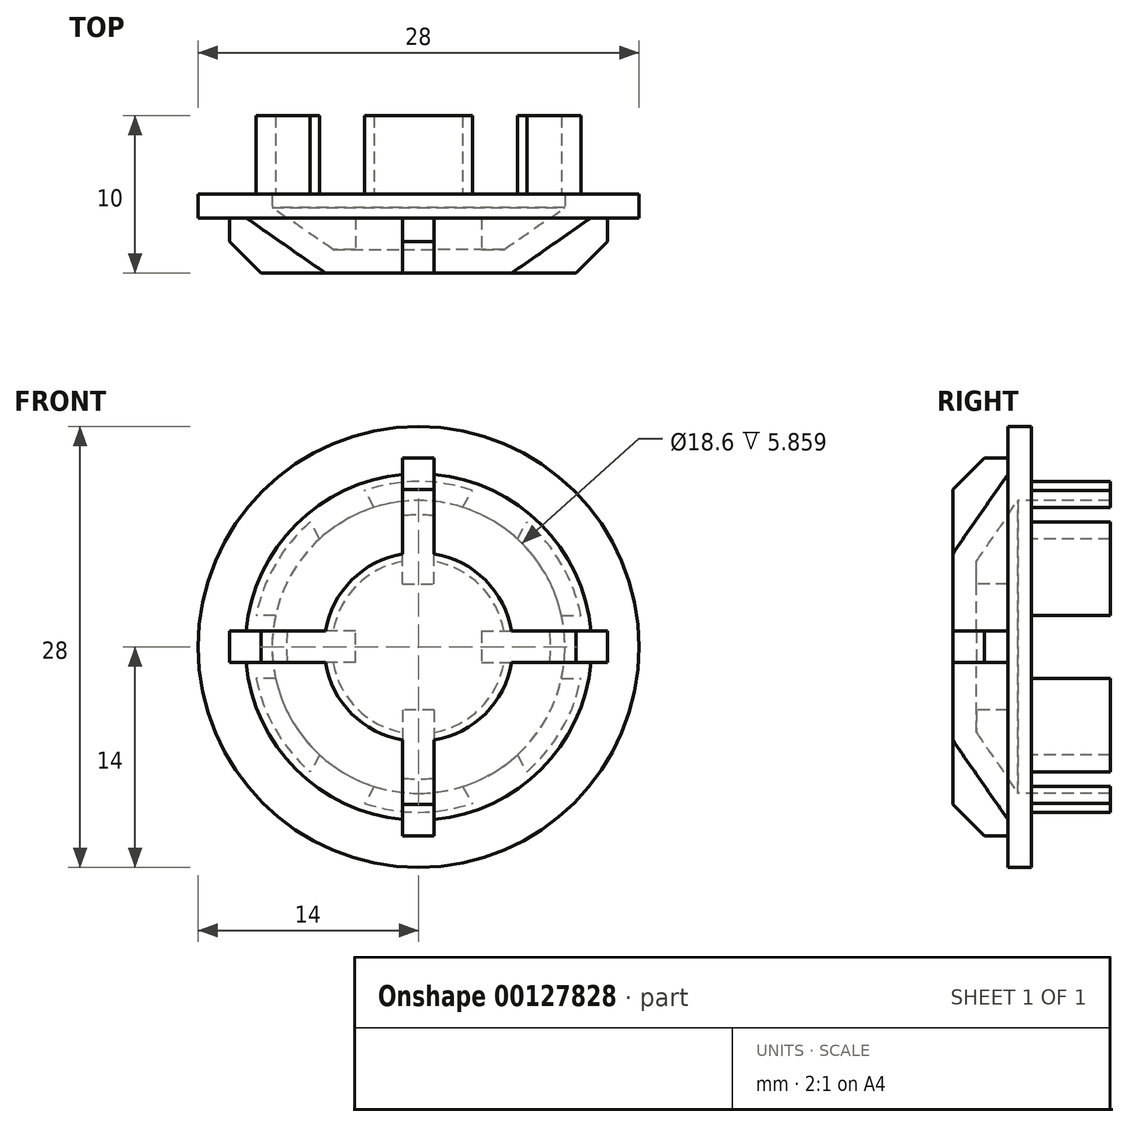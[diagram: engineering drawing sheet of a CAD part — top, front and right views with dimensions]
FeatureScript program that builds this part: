
annotation { "Feature Type Name" : "Feature", "Feature Type Description" : "" }
export const myFeature = defineFeature(function(context is Context, id is Id, definition is map)
    precondition{}
    {
        {
            var Q0;
            Q0=qCreatedBy(makeId("Top.planeOp"),FACE);
            var sketch = newSketch(context, id + "F0", { "sketchPlane" : qUnion([Q0])});
            skLineSegment(sketch, "E0", {"start": v(0, 0) * mm, "end": v(6, 0) * mm});
            skLineSegment(sketch, "E1", {"start": v(6, 0) * mm, "end": v(11, 3.5) * mm});
            skLineSegment(sketch, "E2", {"start": v(11, 3.5) * mm, "end": v(14, 3.5) * mm});
            skLineSegment(sketch, "E3", {"start": v(14, 3.5) * mm, "end": v(14, 5) * mm});
            skLineSegment(sketch, "E4", {"start": v(14, 5) * mm, "end": v(10.5, 5) * mm});
            skLineSegment(sketch, "E5", {"start": v(10.5, 5) * mm, "end": v(10.5, 10) * mm});
            skLineSegment(sketch, "E6", {"start": v(10.5, 10) * mm, "end": v(9.3, 10) * mm});
            skLineSegment(sketch, "E7", {"start": v(9.3, 10) * mm, "end": v(9.3, 4.14) * mm});
            skLineSegment(sketch, "E8", {"start": v(9.3, 4.14) * mm, "end": v(5.53, 1.5) * mm});
            skLineSegment(sketch, "E9", {"start": v(5.53, 1.5) * mm, "end": v(0, 1.5) * mm});
            skLineSegment(sketch, "E10", {"start": v(0, 1.5) * mm, "end": v(0, 0) * mm});
            skLineSegment(sketch, "E11", {"start": v(0, 0) * mm, "end": v(0, 11.38) * mm, "construction": true});
            skSolve(sketch);
        }
        {
            var Q0;
            Q0 = qSketchRegion(id + "F0", true);
            var Q1;
            Q1 = qConstructionFilter(qBodyType(qCreatedBy(id + "F0" ,EDGE), BodyType.WIRE), ConstructionObject.NO);
            var Q2;
            Q2=sQuery(id+"F0.wireOp",EDGE,"E11");
            revolve(context, id + "F1", {"entities" : qUnion([Q0]), "surfaceEntities" : qUnion([Q1]), "axis" : qUnion([Q2]), "revolveType" : RevolveType.FULL});
        }
        {
            var Q0;
            Q0=makeQuery(id+"F1.opRevolve","SWEPT_FACE",FACE,{"disambiguationData":[OSD([sQuery(id+"F0.wireOp",EDGE,"E6")])]});
            var sketch = newSketch(context, id + "F2", { "sketchPlane" : qUnion([Q0])});
            skLineSegment(sketch, "E12.bottom", {"start": v(7.95, 2) * mm, "end": v(11.94, 2) * mm});
            skLineSegment(sketch, "E12.top", {"start": v(7.95, -2) * mm, "end": v(11.94, -2) * mm});
            skLineSegment(sketch, "E12.left", {"start": v(7.95, 2) * mm, "end": v(7.95, -2) * mm});
            skLineSegment(sketch, "E12.right", {"start": v(11.94, 2) * mm, "end": v(11.94, -2) * mm});
            skLineSegment(sketch, "E13.1.0", {"start": v(2.24, 7.88) * mm, "end": v(4.24, 11.34) * mm});
            skLineSegment(sketch, "E13.1.1", {"start": v(5.7, 5.88) * mm, "end": v(7.7, 9.34) * mm});
            skLineSegment(sketch, "E13.1.2", {"start": v(2.24, 7.88) * mm, "end": v(5.7, 5.88) * mm});
            skLineSegment(sketch, "E13.1.3", {"start": v(4.24, 11.34) * mm, "end": v(7.7, 9.34) * mm});
            skLineSegment(sketch, "E13.2.0", {"start": v(-5.7, 5.88) * mm, "end": v(-7.7, 9.34) * mm});
            skLineSegment(sketch, "E13.2.1", {"start": v(-2.24, 7.88) * mm, "end": v(-4.24, 11.34) * mm});
            skLineSegment(sketch, "E13.2.2", {"start": v(-5.7, 5.88) * mm, "end": v(-2.24, 7.88) * mm});
            skLineSegment(sketch, "E13.2.3", {"start": v(-7.7, 9.34) * mm, "end": v(-4.24, 11.34) * mm});
            skLineSegment(sketch, "E13.3.0", {"start": v(-7.95, -2) * mm, "end": v(-11.94, -2) * mm});
            skLineSegment(sketch, "E13.3.1", {"start": v(-7.95, 2) * mm, "end": v(-11.94, 2) * mm});
            skLineSegment(sketch, "E13.3.2", {"start": v(-7.95, -2) * mm, "end": v(-7.95, 2) * mm});
            skLineSegment(sketch, "E13.3.3", {"start": v(-11.94, -2) * mm, "end": v(-11.94, 2) * mm});
            skLineSegment(sketch, "E13.4.0", {"start": v(-2.24, -7.88) * mm, "end": v(-4.24, -11.34) * mm});
            skLineSegment(sketch, "E13.4.1", {"start": v(-5.7, -5.88) * mm, "end": v(-7.7, -9.34) * mm});
            skLineSegment(sketch, "E13.4.2", {"start": v(-2.24, -7.88) * mm, "end": v(-5.7, -5.88) * mm});
            skLineSegment(sketch, "E13.4.3", {"start": v(-4.24, -11.34) * mm, "end": v(-7.7, -9.34) * mm});
            skLineSegment(sketch, "E13.5.0", {"start": v(5.7, -5.88) * mm, "end": v(7.7, -9.34) * mm});
            skLineSegment(sketch, "E13.5.1", {"start": v(2.24, -7.88) * mm, "end": v(4.24, -11.34) * mm});
            skLineSegment(sketch, "E13.5.2", {"start": v(5.7, -5.88) * mm, "end": v(2.24, -7.88) * mm});
            skLineSegment(sketch, "E13.5.3", {"start": v(7.7, -9.34) * mm, "end": v(4.24, -11.34) * mm});
            skPoint(sketch, "E13.center", {"position": v(0, 0) * mm});
            skSolve(sketch);
        }
        {
            var Q0;
            Q0 = qSketchRegion(id + "F2", true);
            var Q1;
            Q1=makeQuery(id+"F1.opRevolve","SWEPT_FACE",FACE,{"disambiguationData":[OSD([sQuery(id+"F0.wireOp",EDGE,"E4")])]});
            extrude(context, id + "F3", {"entities" : qUnion([Q0]), "operationType" : NewBodyOperationType.REMOVE, "endBound" : BoundingType.UP_TO_SURFACE, "oppositeDirection" : true, "endBoundEntityFace" : qUnion([Q1]), "depth" : 25 * mm});
        }
        {
            var Q0;
            Q0=makeQuery(id+"F1.opRevolve","SWEPT_FACE",FACE,{"disambiguationData":[OSD([sQuery(id+"F0.wireOp",EDGE,"E0")])]});
            var sketch = newSketch(context, id + "F4", { "sketchPlane" : qUnion([Q0])});
            skLineSegment(sketch, "E14.bottom", {"start": v(-12, 1) * mm, "end": v(-4, 1) * mm});
            skLineSegment(sketch, "E14.top", {"start": v(-12, -1) * mm, "end": v(-4, -1) * mm});
            skLineSegment(sketch, "E14.left", {"start": v(-12, 1) * mm, "end": v(-12, -1) * mm});
            skLineSegment(sketch, "E14.right", {"start": v(-4, 1) * mm, "end": v(-4, -1) * mm});
            skLineSegment(sketch, "E15.1.0", {"start": v(-1, -12) * mm, "end": v(-1, -4) * mm});
            skLineSegment(sketch, "E15.1.1", {"start": v(1, -12) * mm, "end": v(1, -4) * mm});
            skLineSegment(sketch, "E15.1.2", {"start": v(-1, -12) * mm, "end": v(1, -12) * mm});
            skLineSegment(sketch, "E15.1.3", {"start": v(-1, -4) * mm, "end": v(1, -4) * mm});
            skLineSegment(sketch, "E15.2.0", {"start": v(12, -1) * mm, "end": v(4, -1) * mm});
            skLineSegment(sketch, "E15.2.1", {"start": v(12, 1) * mm, "end": v(4, 1) * mm});
            skLineSegment(sketch, "E15.2.2", {"start": v(12, -1) * mm, "end": v(12, 1) * mm});
            skLineSegment(sketch, "E15.2.3", {"start": v(4, -1) * mm, "end": v(4, 1) * mm});
            skLineSegment(sketch, "E15.3.0", {"start": v(1, 12) * mm, "end": v(1, 4) * mm});
            skLineSegment(sketch, "E15.3.1", {"start": v(-1, 12) * mm, "end": v(-1, 4) * mm});
            skLineSegment(sketch, "E15.3.2", {"start": v(1, 12) * mm, "end": v(-1, 12) * mm});
            skLineSegment(sketch, "E15.3.3", {"start": v(1, 4) * mm, "end": v(-1, 4) * mm});
            skPoint(sketch, "E15.center", {"position": v(0, 0) * mm});
            skSolve(sketch);
        }
        {
            var Q0;
            Q0 = qSketchRegion(id + "F4", true);
            var Q1;
            Q1=makeQuery(id+"F1.opRevolve","SWEPT_FACE",FACE,{"disambiguationData":[OSD([sQuery(id+"F0.wireOp",EDGE,"E2")])]});
            extrude(context, id + "F5", {"entities" : qUnion([Q0]), "operationType" : NewBodyOperationType.ADD, "endBound" : BoundingType.UP_TO_SURFACE, "oppositeDirection" : true, "endBoundEntityFace" : qUnion([Q1]), "depth" : 25 * mm});
        }
        {
            var Q0;
            Q0=makeQuery(id+"F5.opExtrude","CAP_EDGE",EDGE,{"disambiguationData":[OSD([sQuery(id+"F4.wireOp",EDGE,"E14.left")])],"isStart":true});
            var Q1;
            Q1=makeQuery(id+"F5.opExtrude","CAP_EDGE",EDGE,{"disambiguationData":[OSD([sQuery(id+"F4.wireOp",EDGE,"E15.1.2")])],"isStart":true});
            var Q2;
            Q2=makeQuery(id+"F5.opExtrude","CAP_EDGE",EDGE,{"disambiguationData":[OSD([sQuery(id+"F4.wireOp",EDGE,"E15.2.2")])],"isStart":true});
            var Q3;
            Q3=makeQuery(id+"F5.opExtrude","CAP_EDGE",EDGE,{"disambiguationData":[OSD([sQuery(id+"F4.wireOp",EDGE,"E15.3.2")])],"isStart":true});
            chamfer(context, id + "F6", {"entities" : qUnion([Q0, Q1, Q2, Q3]), "width" : 2 * mm, "tangentPropagation" : true});
        }
    });
